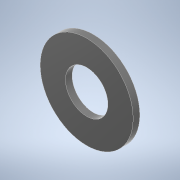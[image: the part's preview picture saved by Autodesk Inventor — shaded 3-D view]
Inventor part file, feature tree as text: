
AUTODESK INVENTOR PART (.ipt)
format: ipt  version: 2022 (Build 260153000, 153)  size: 100,352 bytes
history: native  units: mm
features: extrude x1, sketch x1
ambient origin geometry x8: Origin, YZ Plane, XZ Plane, XY Plane, X Axis, Y Axis, Z Axis, Center Point
bodies: Solid1 (feature_tree)
feature tree (2):
  extrude  "Extrusion1"  Depth=0.5mm
  sketch  "Sketch1"  dims[d0=3.2mm d1=7.0mm d2=0.5mm d3=0.0mm]
